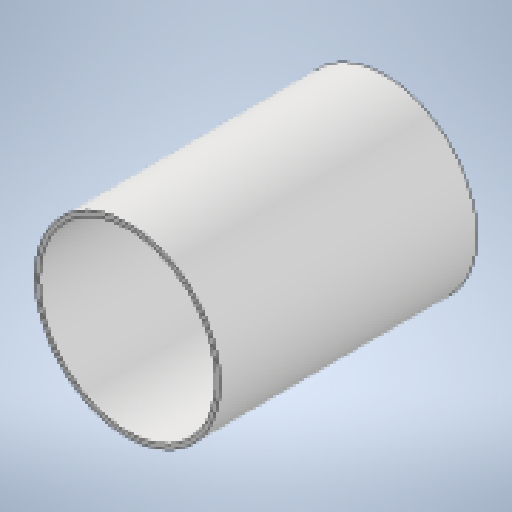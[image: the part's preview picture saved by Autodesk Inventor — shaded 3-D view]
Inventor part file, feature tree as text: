
AUTODESK INVENTOR PART (.ipt)
format: ipt  version: 2025.1 (Build 291241020, 241B)  size: 314,880 bytes
history: native  units: mm
features: extrude x1, sketch x1
ambient origin geometry x8: Origin, YZ Plane, XZ Plane, XY Plane, X Axis, Y Axis, Z Axis, Center Point
bodies: Solid1 (feature_tree)
feature tree (2):
  extrude  "Extrusion1"  Depth=220.0mm
  sketch  "Sketch1"  dims[d0=159.0mm d1=4.0mm d2=220.0mm d3=0.0mm]
